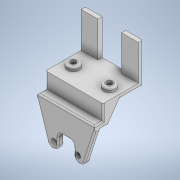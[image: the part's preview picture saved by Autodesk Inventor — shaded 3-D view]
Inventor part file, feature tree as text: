
AUTODESK INVENTOR PART (.ipt)
format: ipt  version: 2020 (Build 240168000, 168)  size: 434,688 bytes
history: native  units: in
note: dims shown in document units (in); Inventor stores cm internally (conversion verified against a paired STEP export)
features: extrude x13, sketch x13, fillet x4
ambient origin geometry x8: Origin, YZ Plane, XZ Plane, XY Plane, X Axis, Y Axis, Z Axis, Center Point
bodies: Solid1 (feature_tree)
feature tree (30):
  extrude  "Extrusion1"  Depth=1.2756in
  extrude  "Extrusion4"  Depth=0.8465in
  extrude  "Extrusion5"  Depth=0.8465in
  extrude  "Extrusion6"  Depth=0.3346in
  extrude  "Extrusion7"  Depth=0.1181in TaperAngle=0.0deg
  extrude  "Extrusion8"  Depth=0.1575in
  extrude  "Extrusion15"  Depth=0.2362in
  extrude  "Extrusion16"  Depth=0.1181in TaperAngle=0.0deg
  extrude  "Extrusion17"  Depth=1.5748in TaperAngle=0.0deg
  extrude  "Extrusion18"  Depth=0.1181in
  extrude  "Extrusion19"  Depth=0.1181in
  extrude  "Extrusion20"  Depth=0.1575in
  fillet  "Fillet3"  Radius=0.1181in
  fillet  "Fillet4"  Radius=0.1181in
  extrude  "Extrusion21"  Depth=0.0591in TaperAngle=0.0deg
  fillet  "Fillet5"  Radius=0.1575in
  fillet  "Fillet6"  Radius=0.2362in
  sketch  "Sketch1"  dims[d0=1.6142in d1=1.2756in]
  sketch  "Sketch4"  dims[d2=0.1181in d3=0.0in d12=0.8465in]
  sketch  "Sketch5"  dims[d13=0.1181in d14=0.0in d15=0.8465in]
  sketch  "Sketch6"  dims[d16=0.1181in d17=0.0in d20=0.3346in]
  sketch  "Sketch7"  dims[d21=0.3346in d22=0.1181in d23=0.0in]
  sketch  "Sketch8"  dims[d24=0.1575in d25=0.1575in]
  sketch  "Sketch16"  dims[d26=0.2362in d27=0.0in d28=0.2362in]
  sketch  "Sketch17"  dims[d29=0.2362in d30=0.1181in d31=0.0in]
  sketch  "Sketch18"  dims[d56=0.1575in d57=1.5748in d58=0.0in]
  sketch  "Sketch19"  dims[d59=0.4724in d60=0.1181in]
  sketch  "Sketch20"  dims[d61=0.4724in d62=0.1181in]
  sketch  "Sketch21"  dims[d63=1.0in d64=0.0in d65=0.1575in d66=0.1181in d67=0.1181in]
  sketch  "Sketch22"  dims[d68=0.1181in d69=0.4724in d70=0.0in d71=0.1575in d72=0.2362in d73=0.0in d74=0.1575in d75=0.1181in d76=0.1181in d77=0.9843in d78=0.0in d79=0.1575in d80=0.1575in d81=0.4331in d82=0.4724in d83=0.9843in d84=0.0in d85=0.1181in d86=0.1575in d87=1.9685in d88=0.0in d89=0.0394in d90=0.0591in d91=0.1969in d92=0.1969in d10=0.0197in d11=0.0344in]
